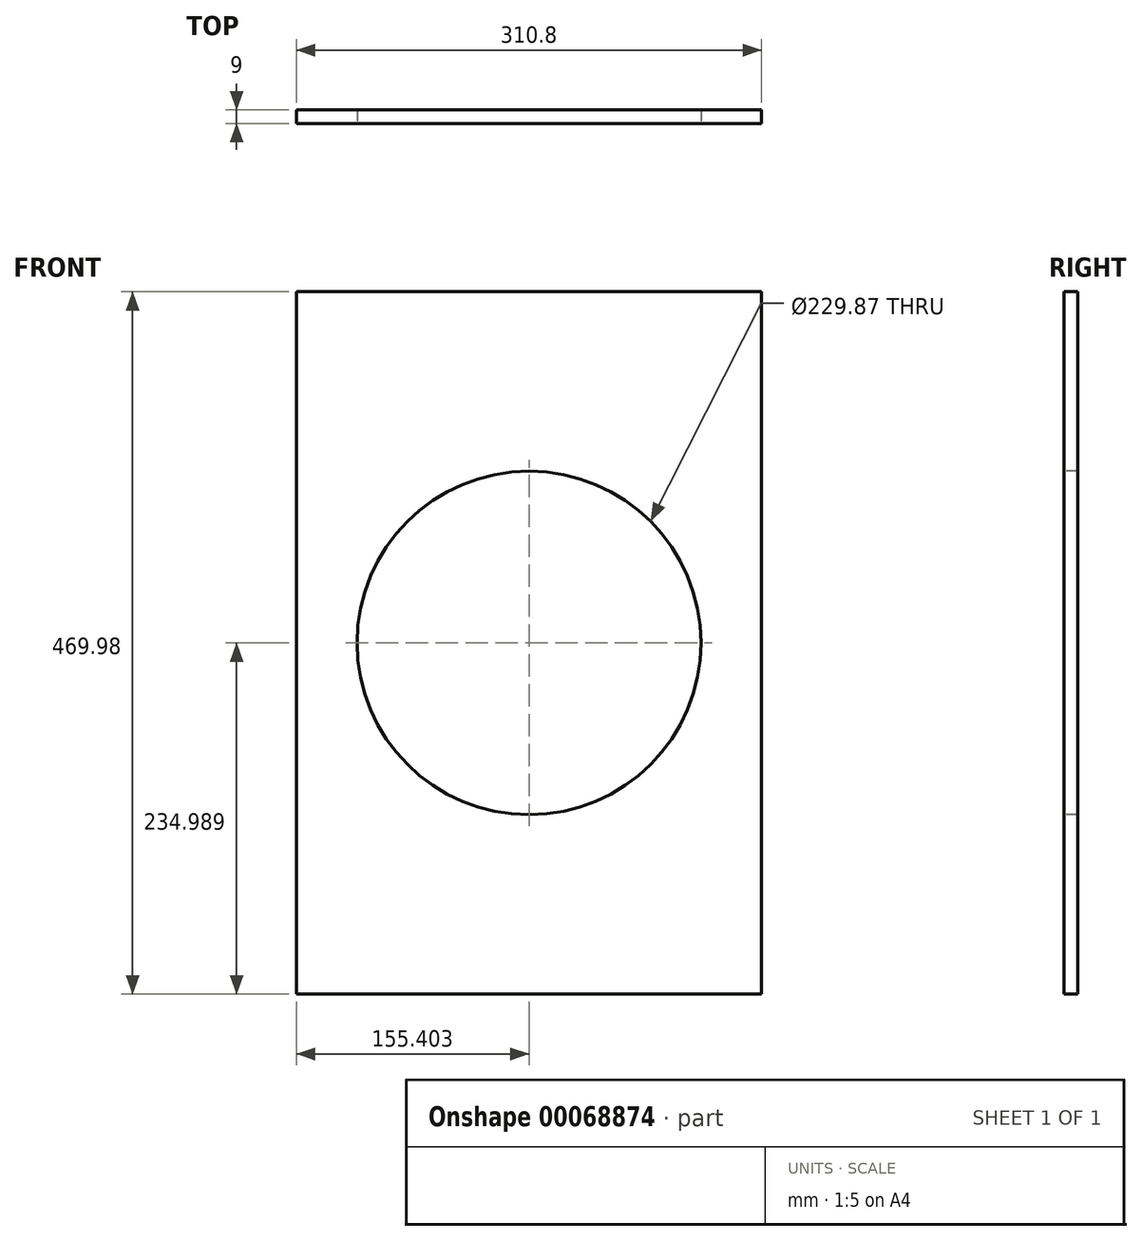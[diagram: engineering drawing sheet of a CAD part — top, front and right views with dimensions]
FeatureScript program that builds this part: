
annotation { "Feature Type Name" : "Feature", "Feature Type Description" : "" }
export const myFeature = defineFeature(function(context is Context, id is Id, definition is map)
    precondition{}
    {
        {
            assignVariable(context, id + "F0", {"name" : "MaterialThickness", "minmax" : VariableMinMaxSelection.MINIMUM, "extendEntities" : false, "measureFromAxis" : false, "distance" : 0 * mm, "xOffset" : 0 * mm, "yOffset" : 0 * mm, "zOffset" : 0 * mm, "componentSelector" : AxisWithCustom.DISTANCE, "customOffset" : 0 * mm, "radius" : false, "description" : "", "measurementMode" : VariableMeasurementMode.DISTANCE, "anyValue" : 9 * mm, "mode" : VariableMode.ASSIGNED});
        }
        {
            var Q0;
            Q0=qCreatedBy(makeId("Front.planeOp"),FACE);
            var sketch = newSketch(context, id + "F1", { "sketchPlane" : qUnion([Q0])});
            skLineSegment(sketch, "E0.bottom", {"start": v(-135.86, 321.38) * mm, "end": v(174.94, 321.38) * mm});
            skLineSegment(sketch, "E0.top", {"start": v(-135.86, -148.6) * mm, "end": v(174.94, -148.6) * mm});
            skLineSegment(sketch, "E0.left", {"start": v(-135.86, 321.38) * mm, "end": v(-135.86, -148.6) * mm});
            skLineSegment(sketch, "E0.right", {"start": v(174.94, 321.38) * mm, "end": v(174.94, -148.6) * mm});
            skSolve(sketch);
        }
        {
            var Q0;
            Q0 = qSketchRegion(id + "F1", true);
            extrude(context, id + "F2", {"entities" : qUnion([Q0]), "depth" : getVariable(context, 'MaterialThickness')});
        }
        {
            var Q0;
            Q0=makeQuery(id+"F2.opExtrude","CAP_FACE",FACE,{"disambiguationData":[OSD([sQuery(id+"F1.wireOp",EDGE,"E0.bottom"),sQuery(id+"F1.wireOp",EDGE,"E0.top"),sQuery(id+"F1.wireOp",EDGE,"E0.left"),sQuery(id+"F1.wireOp",EDGE,"E0.right")])],"isStart":false});
            var sketch = newSketch(context, id + "F3", { "sketchPlane" : qUnion([Q0])});
            skLineSegment(sketch, "E1", {"start": v(19.54, 321.38) * mm, "end": v(19.54, -148.6) * mm, "construction": true});
            skLineSegment(sketch, "E2", {"start": v(174.94, 86.39) * mm, "end": v(-135.86, 86.39) * mm, "construction": true});
            skCircle(sketch, "E3", {"center": v(19.54, 86.39) * mm, "radius": 114.94 * mm});
            skSolve(sketch);
        }
        {
            var Q0;
            Q0 = qSketchRegion(id + "F3", true);
            extrude(context, id + "F4", {"entities" : qUnion([Q0]), "operationType" : NewBodyOperationType.REMOVE, "endBound" : BoundingType.THROUGH_ALL, "oppositeDirection" : true, "depth" : 25.4 * mm});
        }
    });
